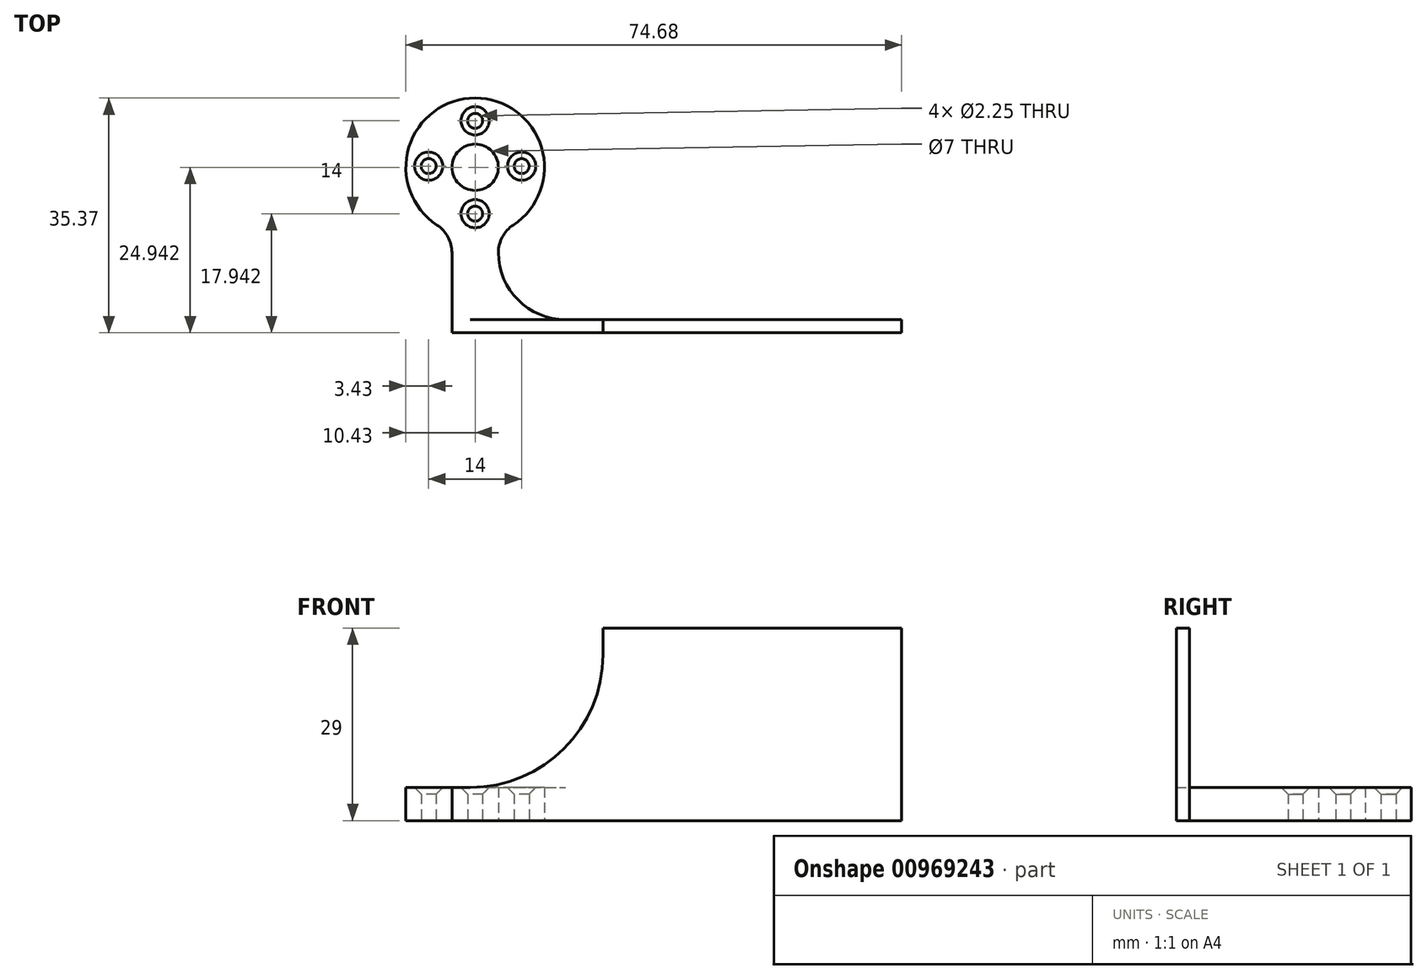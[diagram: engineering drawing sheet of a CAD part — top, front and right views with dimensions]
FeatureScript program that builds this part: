
annotation { "Feature Type Name" : "Feature", "Feature Type Description" : "" }
export const myFeature = defineFeature(function(context is Context, id is Id, definition is map)
    precondition{}
    {
        {
            var Q0;
            Q0=qCreatedBy(makeId("Top.planeOp"),FACE);
            var sketch = newSketch(context, id + "F0", { "sketchPlane" : qUnion([Q0])});
            skLineSegment(sketch, "E0", {"start": v(-3.5, 0) * mm, "end": v(64.25, 0) * mm});
            skLineSegment(sketch, "E1", {"start": v(64.25, 0) * mm, "end": v(64.25, 2) * mm});
            skLineSegment(sketch, "E2", {"start": v(64.25, 2) * mm, "end": v(13.63, 2) * mm});
            skPoint(sketch, "E3.visualSharp", {"position": v(3.5, 2) * mm});
            skArc(sketch, "E3.filletArc", {"start": v(3.5, 12.13) * mm, "mid": v(6.47, 4.97) * mm, "end": v(13.63, 2) * mm});
            skArc(sketch, "E4", {"start": v(5.75, 16.24) * mm, "mid": v(0, 35.37) * mm, "end": v(-5.75, 16.24) * mm});
            skLineSegment(sketch, "E5", {"start": v(-3.5, 0) * mm, "end": v(-3.5, 12.06) * mm});
            skLineSegment(sketch, "E6", {"start": v(3.5, 12.06) * mm, "end": v(3.5, 12.13) * mm});
            skCircle(sketch, "E7", {"center": v(0, 24.94) * mm, "radius": 3.5 * mm});
            skPoint(sketch, "E8.visualSharp", {"position": v(-3.5, 15.12) * mm});
            skArc(sketch, "E8.filletArc", {"start": v(-3.5, 12.06) * mm, "mid": v(-4.1, 14.43) * mm, "end": v(-5.75, 16.24) * mm});
            skPoint(sketch, "E9.visualSharp", {"position": v(3.5, 15.12) * mm});
            skArc(sketch, "E9.filletArc", {"start": v(5.75, 16.24) * mm, "mid": v(4.1, 14.43) * mm, "end": v(3.5, 12.06) * mm});
            skCircle(sketch, "E10", {"center": v(0, 31.94) * mm, "radius": 1.13 * mm});
            skCircle(sketch, "E11.MirrorC", {"center": v(0, 17.94) * mm, "radius": 1.13 * mm});
            skCircle(sketch, "E12", {"center": v(7, 25.11) * mm, "radius": 1.13 * mm});
            skCircle(sketch, "E13.MirrorC", {"center": v(-7, 25.11) * mm, "radius": 1.13 * mm});
            skSolve(sketch);
        }
        {
            var Q0;
            Q0 = qSketchRegion(id + "F0", true);
            extrude(context, id + "F1", {"entities" : qUnion([Q0]), "depth" : 5 * mm, "offsetDistance" : 25 * mm});
        }
        {
            var Q0;
            Q0=makeQuery(id+"F1.opExtrude","CAP_EDGE",EDGE,{"disambiguationData":[OSD([sQuery(id+"F0.wireOp",EDGE,"E10")])],"isStart":false});
            var Q1;
            Q1=makeQuery(id+"F1.opExtrude","CAP_EDGE",EDGE,{"disambiguationData":[OSD([sQuery(id+"F0.wireOp",EDGE,"E12")])],"isStart":false});
            var Q2;
            Q2=makeQuery(id+"F1.opExtrude","CAP_EDGE",EDGE,{"disambiguationData":[OSD([sQuery(id+"F0.wireOp",EDGE,"E13.MirrorC")])],"isStart":false});
            var Q3;
            Q3=makeQuery(id+"F1.opExtrude","CAP_EDGE",EDGE,{"disambiguationData":[OSD([sQuery(id+"F0.wireOp",EDGE,"E11.MirrorC")])],"isStart":false});
            chamfer(context, id + "F2", {"entities" : qUnion([Q0, Q1, Q2, Q3]), "width" : 1 * mm, "tangentPropagation" : true});
        }
        {
            var Q0;
            Q0=qCreatedBy(makeId("Front.planeOp"),FACE);
            var sketch = newSketch(context, id + "F3", { "sketchPlane" : qUnion([Q0])});
            skLineSegment(sketch, "E14", {"start": v(64.25, 0) * mm, "end": v(64.25, 29) * mm});
            skLineSegment(sketch, "E15", {"start": v(64.25, 29) * mm, "end": v(19.25, 29) * mm});
            skLineSegment(sketch, "E16", {"start": v(19.25, 29) * mm, "end": v(19.25, 25) * mm});
            skPoint(sketch, "E17.visualSharp", {"position": v(19.25, 5) * mm});
            skArc(sketch, "E17.filletArc", {"start": v(-0.75, 5) * mm, "mid": v(13.39, 10.86) * mm, "end": v(19.25, 25) * mm});
            skLineSegment(sketch, "E18", {"start": v(-0.75, 5) * mm, "end": v(-3.5, 5) * mm});
            skLineSegment(sketch, "E19", {"start": v(-3.5, 5) * mm, "end": v(-3.5, 0) * mm});
            skLineSegment(sketch, "E20", {"start": v(-3.5, 0) * mm, "end": v(64.25, 0) * mm});
            skSolve(sketch);
        }
        {
            var Q0;
            Q0 = qSketchRegion(id + "F3", true);
            extrude(context, id + "F4", {"entities" : qUnion([Q0]), "operationType" : NewBodyOperationType.ADD, "oppositeDirection" : true, "depth" : 2 * mm, "offsetDistance" : 25 * mm});
        }
    });
